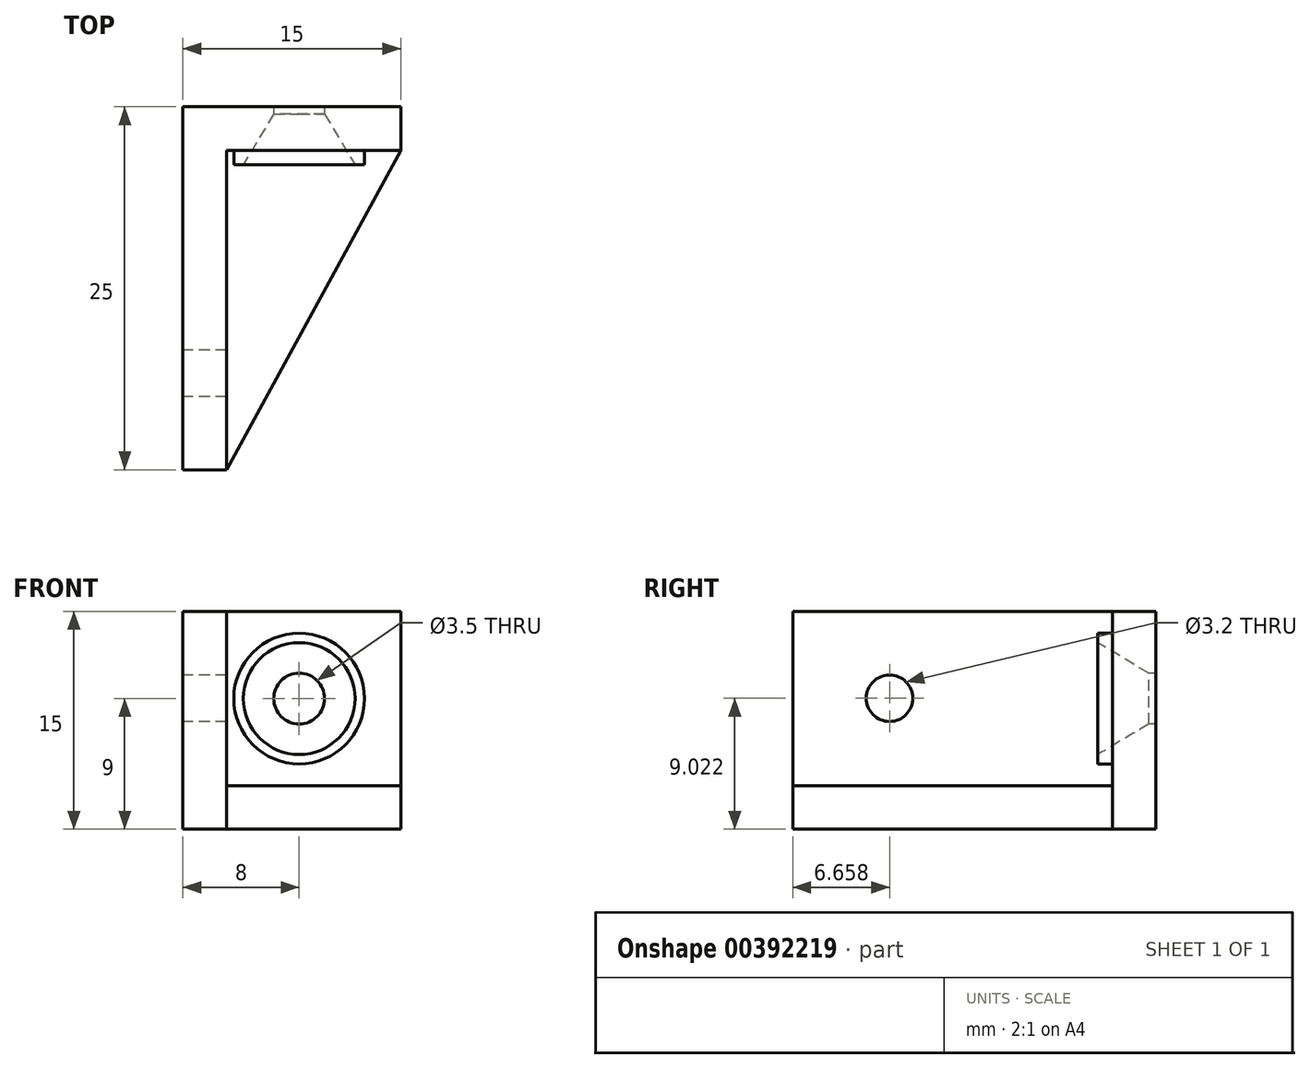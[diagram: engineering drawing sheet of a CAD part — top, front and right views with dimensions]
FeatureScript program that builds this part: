
annotation { "Feature Type Name" : "Feature", "Feature Type Description" : "" }
export const myFeature = defineFeature(function(context is Context, id is Id, definition is map)
    precondition{}
    {
        {
            var Q0;
            Q0=qCreatedBy(makeId("Top.planeOp"),FACE);
            var sketch = newSketch(context, id + "F0", { "sketchPlane" : qUnion([Q0])});
            skPoint(sketch, "E0.middle", {"position": v(0, 0) * mm});
            skLineSegment(sketch, "E1.top", {"start": v(7.5, 12.5) * mm, "end": v(-7.5, 12.5) * mm});
            skLineSegment(sketch, "E1.right", {"start": v(-7.5, -12.5) * mm, "end": v(-7.5, 12.5) * mm});
            skLineSegment(sketch, "E2", {"start": v(-4.5, -12.5) * mm, "end": v(7.5, 9.5) * mm});
            skLineSegment(sketch, "E3", {"start": v(7.5, 12.5) * mm, "end": v(7.5, 9.5) * mm});
            skLineSegment(sketch, "E4", {"start": v(-4.5, -12.5) * mm, "end": v(-7.5, -12.5) * mm});
            skLineSegment(sketch, "E5", {"start": v(-4.5, -12.5) * mm, "end": v(-4.5, 9.5) * mm});
            skLineSegment(sketch, "E6", {"start": v(-4.5, 9.5) * mm, "end": v(7.5, 9.5) * mm});
            skSolve(sketch);
        }
        {
            var Q0;
            {var subQ0=sQuery(id+"F0.wireOp",EDGE,"E2");Q0=makeQuery(id+"F0.imprint","IMPRINT",FACE,{"disambiguationData":[TD([[makeQuery(id+"F0.imprint","IMPRINT",EDGE,{"derivedFrom":subQ0}),1.0]])]});}
            extrude(context, id + "F1", {"entities" : qUnion([Q0]), "depth" : 3 * mm});
        }
        {
            var Q0;
            {var subQ0=sQuery(id+"F0.wireOp",EDGE,"E3");Q0=makeQuery(id+"F0.imprint","IMPRINT",FACE,{"disambiguationData":[TD([[makeQuery(id+"F0.imprint","IMPRINT",EDGE,{"derivedFrom":subQ0}),-1.0]])]});}
            var Q1;
            {var subQ0=sQuery(id+"F0.wireOp",EDGE,"E1.right");var subQ1=sQuery(id+"F0.wireOp",EDGE,"E1.top");var subQ2=makeQuery(id+"F0.imprint","INTERSECT",VERTEX,{"derivedFrom":[subQ1,subQ0]});Q1=makeQuery(id+"F0.imprint","IMPRINT",FACE,{"disambiguationData":[TD([[makeQuery(id+"F0.imprint","IMPRINT",EDGE,{"disambiguationData":[TD([[subQ2,1.0]])],"derivedFrom":subQ1}),1.0]])]});}
            var Q2;
            {var subQ0=sQuery(id+"F0.wireOp",EDGE,"E4");Q2=makeQuery(id+"F0.imprint","IMPRINT",FACE,{"disambiguationData":[TD([[makeQuery(id+"F0.imprint","IMPRINT",EDGE,{"derivedFrom":subQ0}),-1.0]])]});}
            extrude(context, id + "F2", {"entities" : qUnion([Q0, Q1, Q2]), "operationType" : NewBodyOperationType.ADD, "depth" : 15 * mm});
        }
        {
            var Q0;
            Q0=makeQuery(id+"F2.opExtrude","SWEPT_FACE",FACE,{"disambiguationData":[OSD([sQuery(id+"F0.wireOp",EDGE,"E1.right")])]});
            var sketch = newSketch(context, id + "F3", { "sketchPlane" : qUnion([Q0])});
            skLineSegment(sketch, "E7", {"start": v(-4.47, 9.02) * mm, "end": v(12.5, 9.02) * mm, "construction": true});
            skCircle(sketch, "E8", {"center": v(5.84, 9.02) * mm, "radius": 1.6 * mm});
            skSolve(sketch);
        }
        {
            var Q0;
            Q0=qSketchRegion(id+"F3",true);
            extrude(context, id + "F4", {"entities" : qUnion([Q0]), "operationType" : NewBodyOperationType.REMOVE, "oppositeDirection" : true, "depth" : 25 * mm});
        }
        {
            var Q0;
            Q0=makeQuery(id+"F2.opExtrude","SWEPT_FACE",FACE,{"disambiguationData":[OSD([sQuery(id+"F0.wireOp",EDGE,"E6")])]});
            var sketch = newSketch(context, id + "F5", { "sketchPlane" : qUnion([Q0])});
            skCircle(sketch, "E9", {"center": v(0.5, 9) * mm, "radius": 4.5 * mm});
            skLineSegment(sketch, "E10", {"start": v(0.5, 3) * mm, "end": v(0.5, 15) * mm, "construction": true});
            skCircle(sketch, "E11", {"center": v(0.5, 9) * mm, "radius": 1.75 * mm});
            skCircle(sketch, "E12", {"center": v(0.5, 9) * mm, "radius": 3.5 * mm});
            skLineSegment(sketch, "E13", {"start": v(0.5, 9) * mm, "end": v(-7.5, 9) * mm, "construction": true});
            skPoint(sketch, "E13.endSnap0", {"position": v(-4.5, 9) * mm});
            skSolve(sketch);
        }
        {
            var Q0;
            Q0=makeQuery(id+"F5.imprint","IMPRINT",FACE,{"disambiguationData":[TD([[makeQuery(id+"F5.imprint","IMPRINT",EDGE,{"derivedFrom":sQuery(id+"F5.wireOp",EDGE,"E11")}),1.0]])]});
            extrude(context, id + "F6", {"entities" : qUnion([Q0]), "operationType" : NewBodyOperationType.REMOVE, "oppositeDirection" : true, "depth" : 25 * mm});
        }
        {
            var Q0;
            Q0=makeQuery(id+"F5.imprint","IMPRINT",FACE,{"disambiguationData":[TD([[makeQuery(id+"F5.imprint","IMPRINT",EDGE,{"derivedFrom":sQuery(id+"F5.wireOp",EDGE,"E11")}),-1.0]])]});
            var Q1;
            Q1=makeQuery(id+"F5.imprint","IMPRINT",FACE,{"disambiguationData":[TD([[makeQuery(id+"F5.imprint","IMPRINT",EDGE,{"derivedFrom":sQuery(id+"F5.wireOp",EDGE,"E9")}),1.0]])]});
            extrude(context, id + "F7", {"entities" : qUnion([Q0, Q1]), "operationType" : NewBodyOperationType.ADD, "depth" : 1 * mm});
        }
        {
            var Q0;
            Q0=makeQuery(id+"F7.opExtrude","CAP_EDGE",EDGE,{"disambiguationData":[OSD([sQuery(id+"F5.wireOp",EDGE,"E11")])],"isStart":false});
            chamfer(context, id + "F8", {"entities" : qUnion([Q0]), "chamferType" : ChamferType.TWO_OFFSETS, "width1" : 3.5 * mm, "oppositeDirection" : false, "width2" : 2.1 * mm, "tangentPropagation" : true});
        }
    });
